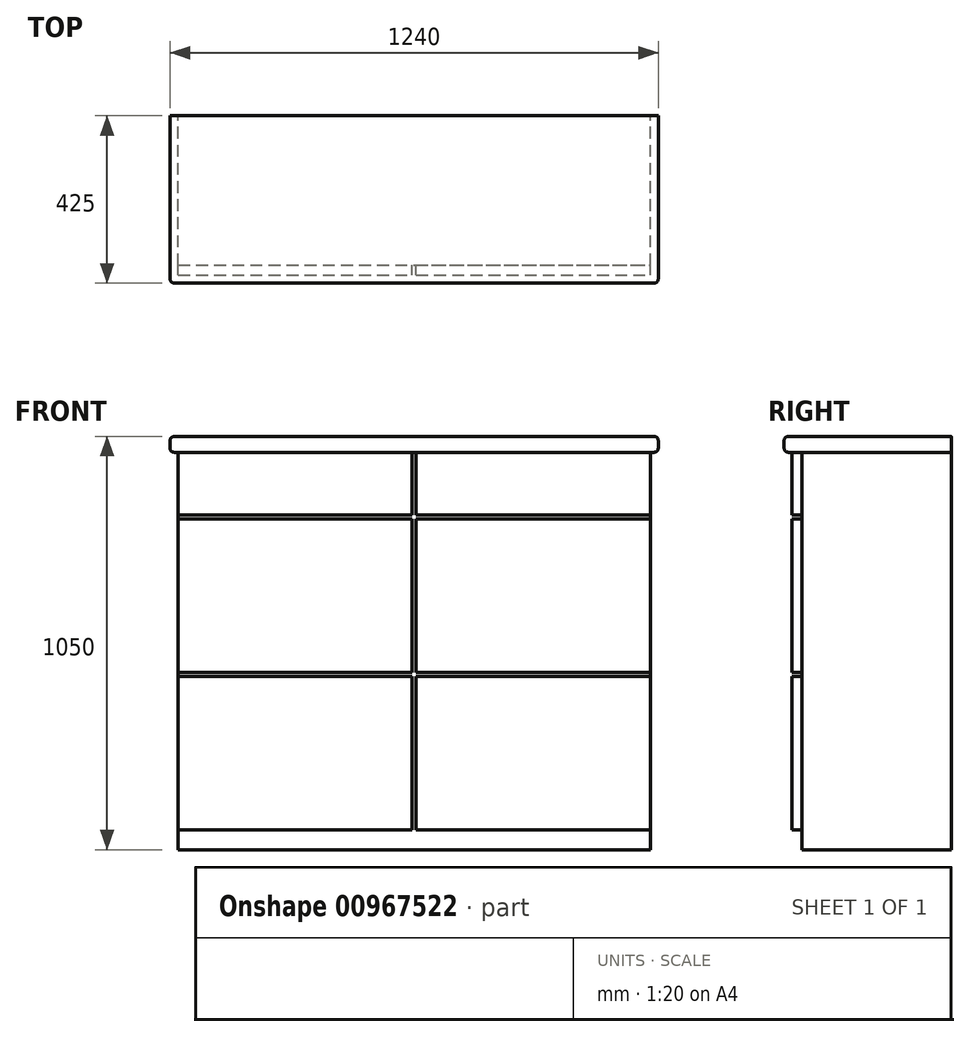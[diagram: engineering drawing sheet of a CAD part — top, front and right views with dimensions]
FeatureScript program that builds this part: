
annotation { "Feature Type Name" : "Feature", "Feature Type Description" : "" }
export const myFeature = defineFeature(function(context is Context, id is Id, definition is map)
    precondition{}
    {
        {
            assignVariable(context, id + "F0", {"variableType" : VariableType.LENGTH, "name" : "H", "lengthValue" : 1050 * mm});
        }
        {
            var Q0;
            Q0=qCreatedBy(makeId("Top.planeOp"),FACE);
            var sketch = newSketch(context, id + "F1", { "sketchPlane" : qUnion([Q0])});
            skLineSegment(sketch, "E0.bottom", {"start": v(0, 0) * mm, "end": v(1200, 0) * mm});
            skLineSegment(sketch, "E0.top", {"start": v(0, 380) * mm, "end": v(1200, 380) * mm});
            skLineSegment(sketch, "E0.left", {"start": v(0, 0) * mm, "end": v(0, 380) * mm});
            skLineSegment(sketch, "E0.right", {"start": v(1200, 0) * mm, "end": v(1200, 380) * mm});
            skSolve(sketch);
        }
        {
            var Q0;
            Q0=makeQuery(id+"F1.imprint","IMPRINT",FACE,{"disambiguationData":[TD([[makeQuery(id+"F1.imprint","IMPRINT",EDGE,{"derivedFrom":sQuery(id+"F1.wireOp",EDGE,"E0.bottom")}),1.0]])]});
            extrude(context, id + "F2", {"entities" : qUnion([Q0]), "depth" : getVariable(context, 'H') - 40 * mm, "offsetDistance" : 25 * mm});
        }
        {
            var Q0;
            Q0=makeQuery(id+"F2.opExtrude","SWEPT_FACE",FACE,{"disambiguationData":[OSD([sQuery(id+"F1.wireOp",EDGE,"E0.bottom")])]});
            var sketch = newSketch(context, id + "F3", { "sketchPlane" : qUnion([Q0])});
            skLineSegment(sketch, "E1.bottom", {"start": v(0, 50) * mm, "end": v(595, 50) * mm});
            skLineSegment(sketch, "E1.top", {"start": v(0, 440) * mm, "end": v(595, 440) * mm});
            skLineSegment(sketch, "E1.left", {"start": v(0, 50) * mm, "end": v(0, 440) * mm});
            skLineSegment(sketch, "E1.right", {"start": v(595, 50) * mm, "end": v(595, 440) * mm});
            skLineSegment(sketch, "E2.bottom", {"start": v(605, 50) * mm, "end": v(1200, 50) * mm});
            skLineSegment(sketch, "E2.top", {"start": v(605, 440) * mm, "end": v(1200, 440) * mm});
            skLineSegment(sketch, "E2.left", {"start": v(605, 50) * mm, "end": v(605, 440) * mm});
            skLineSegment(sketch, "E2.right", {"start": v(1200, 50) * mm, "end": v(1200, 440) * mm});
            skLineSegment(sketch, "E3.bottom", {"start": v(0, 450) * mm, "end": v(595, 450) * mm});
            skLineSegment(sketch, "E3.top", {"start": v(0, 840) * mm, "end": v(595, 840) * mm});
            skLineSegment(sketch, "E3.left", {"start": v(0, 450) * mm, "end": v(0, 840) * mm});
            skLineSegment(sketch, "E3.right", {"start": v(595, 450) * mm, "end": v(595, 840) * mm});
            skLineSegment(sketch, "E4.bottom", {"start": v(605, 450) * mm, "end": v(1200, 450) * mm});
            skLineSegment(sketch, "E4.top", {"start": v(605, 840) * mm, "end": v(1200, 840) * mm});
            skLineSegment(sketch, "E4.left", {"start": v(605, 450) * mm, "end": v(605, 840) * mm});
            skLineSegment(sketch, "E4.right", {"start": v(1200, 450) * mm, "end": v(1200, 840) * mm});
            skLineSegment(sketch, "E5.bottom", {"start": v(0, 1010) * mm, "end": v(595, 1010) * mm});
            skLineSegment(sketch, "E5.top", {"start": v(0, 850) * mm, "end": v(595, 850) * mm});
            skLineSegment(sketch, "E5.left", {"start": v(0, 1010) * mm, "end": v(0, 850) * mm});
            skLineSegment(sketch, "E5.right", {"start": v(595, 1010) * mm, "end": v(595, 850) * mm});
            skLineSegment(sketch, "E6.bottom", {"start": v(1200, 1010) * mm, "end": v(605, 1010) * mm});
            skLineSegment(sketch, "E6.top", {"start": v(1200, 850) * mm, "end": v(605, 850) * mm});
            skLineSegment(sketch, "E6.left", {"start": v(1200, 1010) * mm, "end": v(1200, 850) * mm});
            skLineSegment(sketch, "E6.right", {"start": v(605, 1010) * mm, "end": v(605, 850) * mm});
            skSolve(sketch);
        }
        {
            var Q0;
            Q0 = qSketchRegion(id + "F3", true);
            extrude(context, id + "F4", {"entities" : qUnion([Q0]), "depth" : 25 * mm, "offsetDistance" : 25 * mm});
        }
        {
            var Q0;
            Q0=makeQuery(id+"F2.opExtrude","SWEPT_FACE",FACE,{"disambiguationData":[OSD([sQuery(id+"F1.wireOp",EDGE,"E0.right")])]});
            var sketch = newSketch(context, id + "F5", { "sketchPlane" : qUnion([Q0])});
            skLineSegment(sketch, "E7.bottom", {"start": v(380, 1010) * mm, "end": v(-45, 1010) * mm});
            skLineSegment(sketch, "E7.top", {"start": v(380, 1050) * mm, "end": v(-45, 1050) * mm});
            skLineSegment(sketch, "E7.left", {"start": v(380, 1010) * mm, "end": v(380, 1050) * mm});
            skLineSegment(sketch, "E7.right", {"start": v(-45, 1010) * mm, "end": v(-45, 1050) * mm});
            skSolve(sketch);
        }
        {
            var Q0;
            Q0 = qSketchRegion(id + "F5", true);
            var Q1;
            Q1=makeQuery(id+"F2.opExtrude","SWEPT_FACE",FACE,{"disambiguationData":[OSD([sQuery(id+"F1.wireOp",EDGE,"E0.left")])]});
            extrude(context, id + "F6", {"entities" : qUnion([Q0]), "endBound" : BoundingType.UP_TO_SURFACE, "oppositeDirection" : true, "depth" : 25 * mm, "endBoundEntityFace" : qUnion([Q1]), "hasOffset" : true, "offsetDistance" : 20 * mm, "offsetOppositeDirection" : true, "hasSecondDirection" : true, "secondDirectionOppositeDirection" : false, "secondDirectionDepth" : 20 * mm});
        }
        {
            var Q0;
            Q0=makeQuery(id+"F6.opExtrude","SWEPT_FACE",FACE,{"disambiguationData":[OSD([sQuery(id+"F5.wireOp",EDGE,"E7.right")])]});
            var Q1;
            Q1=makeQuery(id+"F6.opExtrude","CAP_EDGE",EDGE,{"disambiguationData":[OSD([sQuery(id+"F5.wireOp",EDGE,"E7.bottom")])],"isStart":true});
            var Q2;
            Q2=makeQuery(id+"F6.opExtrude","CAP_EDGE",EDGE,{"disambiguationData":[OSD([sQuery(id+"F5.wireOp",EDGE,"E7.top")])],"isStart":true});
            var Q3;
            Q3=makeQuery(id+"F6.opExtrude","CAP_EDGE",EDGE,{"disambiguationData":[OSD([sQuery(id+"F5.wireOp",EDGE,"E7.top")])],"isStart":false});
            var Q4;
            Q4=makeQuery(id+"F6.opExtrude","CAP_EDGE",EDGE,{"disambiguationData":[OSD([sQuery(id+"F5.wireOp",EDGE,"E7.bottom")])],"isStart":false});
            fillet(context, id + "F7", {"entities" : qUnion([Q0, Q1, Q2, Q3, Q4]), "tangentPropagation" : true, "radius" : 10 * mm, "defaultsChanged" : false, "vertexSettings" : [], "allowEdgeOverflow" : false});
        }
    });
